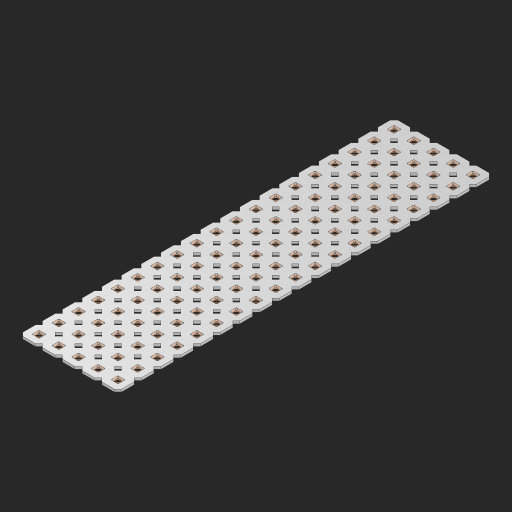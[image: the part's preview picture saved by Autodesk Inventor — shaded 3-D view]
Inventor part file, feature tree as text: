
AUTODESK INVENTOR PART (.ipt)
format: ipt  version: 2023 (Build 270158000, 158)  size: 1,381,888 bytes
history: native  units: in
note: dims shown in document units (in); Inventor stores cm internally (conversion verified against a paired STEP export)
features: other x96, extrude x94, sketch x2, pattern_linear x1
ambient origin geometry x8: Origin, YZ Plane, XZ Plane, XY Plane, X Axis, Y Axis, Z Axis, Center Point
bodies: Solid1 (feature_tree), Body (feature_tree)
feature tree (193):
  pattern_linear  "Rectangular Pattern1"  Spacing1=0.09in  [1 undecoded]
  sketch  "Sketch1"  dims[d1=0.5in]
  sketch  "Sketch2"  dims[d2=0.182in d3=0.09in d4=0.09in d5=0.09in d6=0.09in d7=0.09in d8=0.09in d9=0.09in d10=0.09in d11=0.02in d13=0.0in d14=0.172in d15=0.0625in d16=0.0in d19=0.5in d22=0.5in]
  other  "Srf1"
  other  "Srf126"
  other  "Srf127"
  other  "Srf128"
  other  "Srf129"
  other  "Srf130"
  other  "Srf131"
  other  "Srf250"
  other  "Srf251"
  other  "Srf252"
  other  "Srf253"
  other  "Srf254"
  other  "Srf255"
  other  "Srf256"
  other  "Srf257"
  other  "Srf258"
  other  "Srf259"
  other  "Srf260"
  other  "Srf261"
  other  "Srf268"
  other  "Srf269"
  other  "Srf270"
  other  "Srf271"
  other  "Srf272"
  other  "Srf273"
  other  "Srf274"
  other  "Srf275"
  other  "Srf276"
  other  "Srf277"
  other  "Srf278"
  other  "Srf279"
  other  "Srf280"
  other  "Srf281"
  other  "Srf282"
  other  "Srf283"
  other  "Srf284"
  other  "Srf285"
  other  "Srf286"
  other  "Srf293"
  other  "Srf294"
  other  "Srf295"
  other  "Srf296"
  other  "Srf297"
  other  "Srf298"
  other  "Srf299"
  other  "Srf300"
  other  "Srf301"
  other  "Srf302"
  other  "Srf303"
  other  "Srf304"
  other  "Srf305"
  other  "Srf306"
  other  "Srf307"
  other  "Srf308"
  other  "Srf309"
  other  "Srf310"
  other  "Srf311"
  other  "Srf318"
  other  "Srf319"
  other  "Srf320"
  other  "Srf321"
  other  "Srf322"
  other  "Srf323"
  other  "Srf324"
  other  "Srf325"
  other  "Srf326"
  other  "Srf327"
  other  "Srf328"
  other  "Srf329"
  other  "Srf330"
  other  "Srf331"
  other  "Srf332"
  other  "Srf333"
  other  "Srf334"
  other  "Srf335"
  other  "Srf336"
  other  "Srf343"
  other  "Srf344"
  other  "Srf345"
  other  "Srf346"
  other  "Srf347"
  other  "Srf348"
  other  "Srf349"
  other  "Srf350"
  other  "Srf351"
  other  "Srf352"
  other  "Srf353"
  other  "Srf354"
  other  "Srf355"
  other  "Srf356"
  other  "Srf357"
  other  "Srf358"
  other  "Srf359"
  other  "Srf360"
  other  "Srf361"
  other  "Circle"
  extrude  "ExtrusionSrf126"  Depth=0.09in
  extrude  "ExtrusionSrf127"  Depth=0.09in
  extrude  "ExtrusionSrf128"  Depth=0.09in
  extrude  "ExtrusionSrf129"  Depth=0.09in
  extrude  "ExtrusionSrf130"  Depth=0.09in
  extrude  "ExtrusionSrf131"  Depth=0.09in
  extrude  "ExtrusionSrf250"  Depth=0.09in
  extrude  "ExtrusionSrf251"  Depth=0.02in
  extrude  "ExtrusionSrf252"  TaperAngle=0.0deg  [1 undecoded]
  extrude  "ExtrusionSrf253"  Depth=0.5in
  extrude  "ExtrusionSrf254"  Depth=0.0625in TaperAngle=0.0deg
  extrude  "ExtrusionSrf255"  Depth=0.5in
  extrude  "ExtrusionSrf256"  Depth=0.5in
  extrude  "ExtrusionSrf257"  [1 undecoded]
  extrude  "ExtrusionSrf258"  [1 undecoded]
  extrude  "ExtrusionSrf259"  [1 undecoded]
  extrude  "ExtrusionSrf260"  [1 undecoded]
  extrude  "ExtrusionSrf261"  [1 undecoded]
  extrude  "ExtrusionSrf268"  [1 undecoded]
  extrude  "ExtrusionSrf269"  [1 undecoded]
  extrude  "ExtrusionSrf270"  [1 undecoded]
  extrude  "ExtrusionSrf271"  [1 undecoded]
  extrude  "ExtrusionSrf272"  [1 undecoded]
  extrude  "ExtrusionSrf273"  [1 undecoded]
  extrude  "ExtrusionSrf274"  [1 undecoded]
  extrude  "ExtrusionSrf275"  [1 undecoded]
  extrude  "ExtrusionSrf276"  [1 undecoded]
  extrude  "ExtrusionSrf277"  [1 undecoded]
  extrude  "ExtrusionSrf278"  [1 undecoded]
  extrude  "ExtrusionSrf279"  [1 undecoded]
  extrude  "ExtrusionSrf280"  [1 undecoded]
  extrude  "ExtrusionSrf281"  [1 undecoded]
  extrude  "ExtrusionSrf282"  [1 undecoded]
  extrude  "ExtrusionSrf283"  [1 undecoded]
  extrude  "ExtrusionSrf284"  [1 undecoded]
  extrude  "ExtrusionSrf285"  [1 undecoded]
  extrude  "ExtrusionSrf286"  [1 undecoded]
  extrude  "ExtrusionSrf293"  [1 undecoded]
  extrude  "ExtrusionSrf294"  [1 undecoded]
  extrude  "ExtrusionSrf295"  [1 undecoded]
  extrude  "ExtrusionSrf296"  [1 undecoded]
  extrude  "ExtrusionSrf297"  [1 undecoded]
  extrude  "ExtrusionSrf298"  [1 undecoded]
  extrude  "ExtrusionSrf299"  [1 undecoded]
  extrude  "ExtrusionSrf300"  [1 undecoded]
  extrude  "ExtrusionSrf301"  [1 undecoded]
  extrude  "ExtrusionSrf302"  [1 undecoded]
  extrude  "ExtrusionSrf303"  [1 undecoded]
  extrude  "ExtrusionSrf304"  [1 undecoded]
  extrude  "ExtrusionSrf305"  [1 undecoded]
  extrude  "ExtrusionSrf306"  [1 undecoded]
  extrude  "ExtrusionSrf307"  [1 undecoded]
  extrude  "ExtrusionSrf308"  [1 undecoded]
  extrude  "ExtrusionSrf309"  [1 undecoded]
  extrude  "ExtrusionSrf310"  [1 undecoded]
  extrude  "ExtrusionSrf311"  [1 undecoded]
  extrude  "ExtrusionSrf318"  [1 undecoded]
  extrude  "ExtrusionSrf319"  [1 undecoded]
  extrude  "ExtrusionSrf320"  [1 undecoded]
  extrude  "ExtrusionSrf321"  [1 undecoded]
  extrude  "ExtrusionSrf322"  [1 undecoded]
  extrude  "ExtrusionSrf323"  [1 undecoded]
  extrude  "ExtrusionSrf324"  [1 undecoded]
  extrude  "ExtrusionSrf325"  [1 undecoded]
  extrude  "ExtrusionSrf326"  [1 undecoded]
  extrude  "ExtrusionSrf327"  [1 undecoded]
  extrude  "ExtrusionSrf328"  [1 undecoded]
  extrude  "ExtrusionSrf329"  [1 undecoded]
  extrude  "ExtrusionSrf330"  [1 undecoded]
  extrude  "ExtrusionSrf331"  [1 undecoded]
  extrude  "ExtrusionSrf332"  [1 undecoded]
  extrude  "ExtrusionSrf333"  [1 undecoded]
  extrude  "ExtrusionSrf334"  [1 undecoded]
  extrude  "ExtrusionSrf335"  [1 undecoded]
  extrude  "ExtrusionSrf336"  [1 undecoded]
  extrude  "ExtrusionSrf343"  [1 undecoded]
  extrude  "ExtrusionSrf344"  [1 undecoded]
  extrude  "ExtrusionSrf345"  [1 undecoded]
  extrude  "ExtrusionSrf346"  [1 undecoded]
  extrude  "ExtrusionSrf347"  [1 undecoded]
  extrude  "ExtrusionSrf348"  [1 undecoded]
  extrude  "ExtrusionSrf349"  [1 undecoded]
  extrude  "ExtrusionSrf350"  [1 undecoded]
  extrude  "ExtrusionSrf351"  [1 undecoded]
  extrude  "ExtrusionSrf352"  [1 undecoded]
  extrude  "ExtrusionSrf353"  [1 undecoded]
  extrude  "ExtrusionSrf354"  [1 undecoded]
  extrude  "ExtrusionSrf355"  [1 undecoded]
  extrude  "ExtrusionSrf356"  [1 undecoded]
  extrude  "ExtrusionSrf357"  [1 undecoded]
  extrude  "ExtrusionSrf358"  [1 undecoded]
  extrude  "ExtrusionSrf359"  [1 undecoded]
  extrude  "ExtrusionSrf360"  [1 undecoded]
  extrude  "ExtrusionSrf361"  [1 undecoded]
note: 83 required parameter values undecoded (feature->parameter linkage not recoverable at this tier; creation-order binding heuristic only, values carry confidence <= 0.55)
